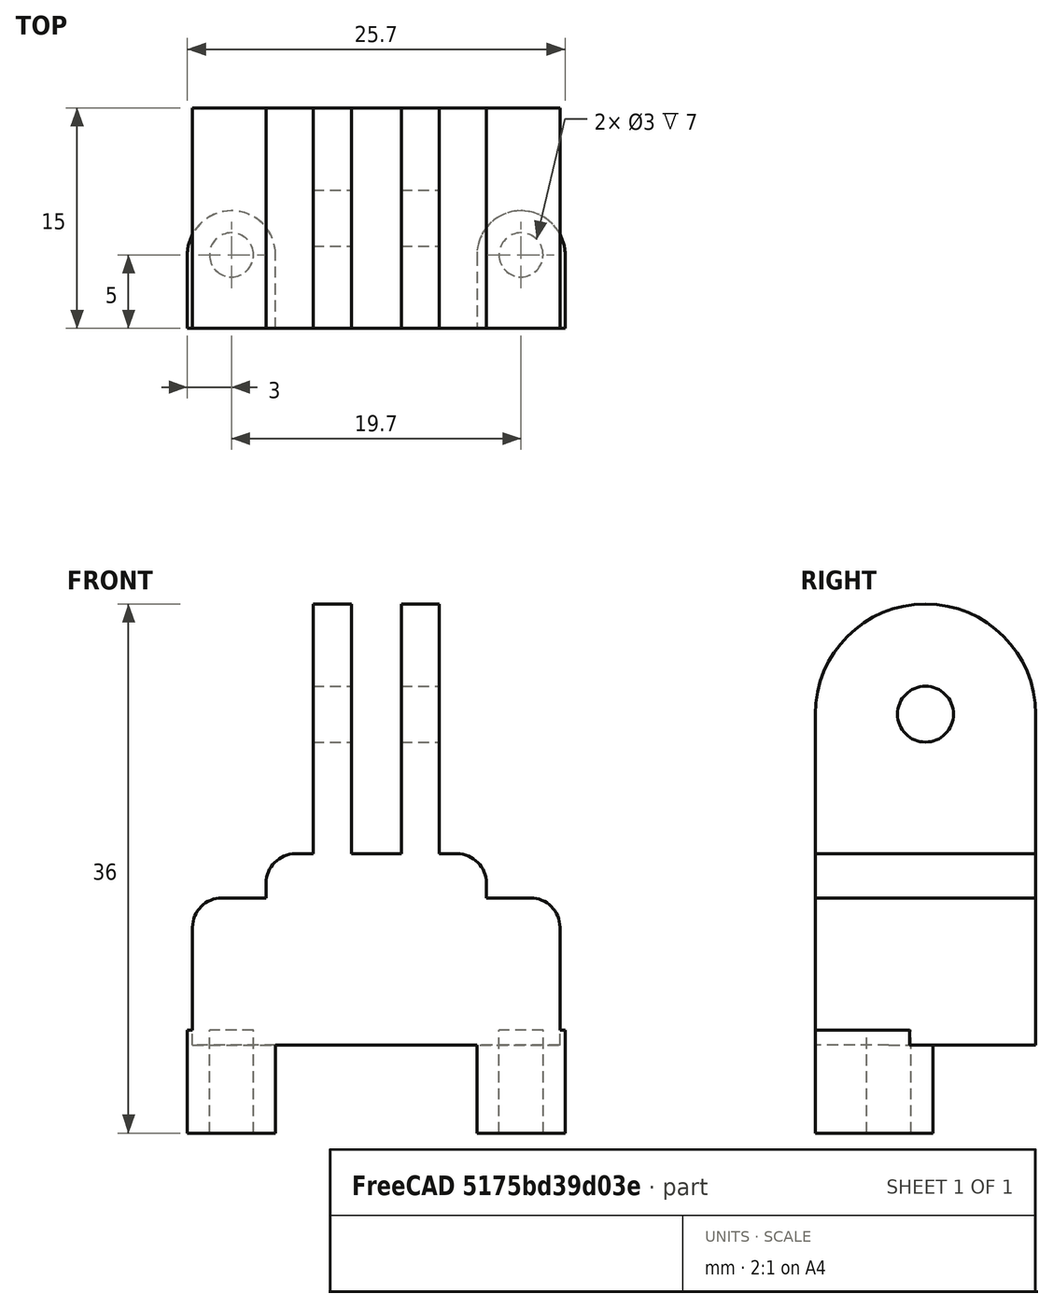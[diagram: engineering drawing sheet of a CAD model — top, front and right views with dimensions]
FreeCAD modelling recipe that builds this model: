
FCSTD DOCUMENT  (FreeCAD 0.19R23578 (Git))
Label: gyvl53l0xv2
License: FreeArt
LicenseURL: http://artlibre.org/licence/lal
objects: Part::MultiFuse×3, Part::Cylinder×2, Part::FeaturePython×2, Part::Box×2, Part::Fillet×2, Spreadsheet::Sheet×1, Part::Feature×1, Part::Cut×1, App::Part×1
note: 13 computed .brp shape members not serialized (recipe doc carries the construction recipe); baked Part::Feature solids carry a one-line shape summary decoded from their .brp

FEATURE [Spreadsheet::Sheet] Spreadsheet  label="p"
  cells = A1=pcb_x; B1(pcb_x)=25; A2=pcb_y; B2(pcb_y)=11; A3=pcb_z; B3(pcb_z)=1.8; A4=hole_dist_x; B4(hole_dist_x)=19.7; A5=hole_off_y; B5(hole_off_y)=5; A6=hole_r; B6(hole_r)=1.5; A7=hole_length; B7(hole_length)=7; A8=hole_stand_r; B8(hole_stand_r)=3; A9=hole_stand_z; B9(hole_stand_z)=6; A10=wall; B10(wall)=3; A11=stick_x; B11(stick_x)==pcb_x; A12=stick_y; B12(stick_y)=15; A13=stick_length; B13(stick_length)=10
FEATURE [Part::Cylinder] Cylinder  label="bolt hole"
  Angle = 360
  AttacherType = Attacher::AttachEngine3D
  Height = 7
  Radius = 1.5
  expr: Radius = <<p>>.hole_r
  expr: Height = <<p>>.hole_length
FEATURE [Part::FeaturePython] Array  label="bolt hole array"  # Draft array (typed FeaturePython)
  Angle = 360
  ArrayType = 0
  Axis = (0,0,1)
  Base = -> Cylinder
  Center = (0,0,0)
  Fuse = false
  IntervalAxis = (0,0,0)
  IntervalX = (19.7,0,0)
  IntervalY = (0,1,0)
  IntervalZ = (0,0,1)
  NumberPolar = 1
  NumberX = 2
  NumberY = 1
  NumberZ = 1
  Placement = pos=(2.65,5,-6) rot=(0,0,1;0rad)
  expr: .Placement.Base.x = (<<p>>.pcb_x - <<p>>.hole_dist_x) / 2
  expr: .IntervalX.x = <<p>>.hole_dist_x
  expr: .Placement.Base.y = <<p>>.hole_off_y
  expr: .Placement.Base.z = -<<p>>.hole_stand_z
FEATURE [Part::Box] Box002  label="stick cube"
  AttacherType = Attacher::AttachEngine3D
  Height = 10
  Length = 25
  Width = 15
  expr: Length = Spreadsheet.stick_x
  expr: Width = <<p>>.stick_y
  expr: Height = <<p>>.stick_length
FEATURE [Part::Feature] Cut001001  label="side 2 cut001"
  Placement = pos=(12.5,7.5,10) rot=(0,0,1;1.5708rad)
  shape: bbox 15 x 15 x 20 mm, 16 faces (baked)
  expr: .Placement.Base.y = <<p>>.stick_y / 2
  expr: .Placement.Base.x = <<p>>.stick_x / 2
  expr: .Placement.Base.z = <<p>>.stick_length
FEATURE [Part::Fillet] Fillet  label="stick cube fillet"
  Base = -> Box002
  Edges = 2 edges r=2: [Edge2,Edge6]
FEATURE [Part::MultiFuse] Fusion  label="holder fusion"
  Shapes = -> [Cut001001,Fillet]
FEATURE [Part::Fillet] Fillet001  label="holder fillet"
  Base = -> Fusion
  Edges = 2 edges r=2: [Edge47,Edge48]
FEATURE [Part::Cylinder] Cylinder001  label="bolt stand"
  Angle = 360
  AttacherType = Attacher::AttachEngine3D
  Height = 7
  Radius = 3
  expr: Height = <<p>>.hole_length
  expr: Radius = <<p>>.hole_stand_r
FEATURE [Part::Box] Box  label="stand cube"
  AttacherType = Attacher::AttachEngine3D
  Height = 7
  Length = 6
  Placement = pos=(-3,-5,0) rot=(0,0,1;0rad)
  Width = 5
  expr: Height = <<p>>.hole_length
  expr: Width = <<p>>.hole_off_y
  expr: Length = <<p>>.hole_stand_r * 2
  expr: .Placement.Base.x = -<<p>>.hole_stand_r
  expr: .Placement.Base.y = -<<p>>.hole_off_y
FEATURE [Part::MultiFuse] Fusion002  label="stand fusion"
  Shapes = -> [Box,Cylinder001]
FEATURE [Part::FeaturePython] Array001  label="bolt stand array"  # Draft array (typed FeaturePython)
  Angle = 360
  ArrayType = 0
  Axis = (0,0,1)
  Base = -> Fusion002
  Center = (0,0,0)
  Fuse = false
  IntervalAxis = (0,0,0)
  IntervalX = (19.7,0,0)
  IntervalY = (0,1,0)
  IntervalZ = (0,0,1)
  NumberPolar = 1
  NumberX = 2
  NumberY = 1
  NumberZ = 1
  Placement = pos=(2.65,5,-6) rot=(0,0,1;0rad)
  expr: .Placement.Base.y = <<p>>.hole_off_y
  expr: .IntervalX.x = <<p>>.hole_dist_x
  expr: .Placement.Base.x = (<<p>>.pcb_x - <<p>>.hole_dist_x) / 2
  expr: .Placement.Base.z = -<<p>>.hole_stand_z
FEATURE [Part::MultiFuse] Fusion001  label="sensor fusion"
  Shapes = -> [Array001,Fillet001]
FEATURE [Part::Cut] Cut  label="sensor cut"
  Base = -> Fusion001
  Tool = -> Array
FEATURE [App::Part] Part  label="gyvl53l0xv2 sensor part"
  Group = -> [Cut]
  Origin = -> Origin
